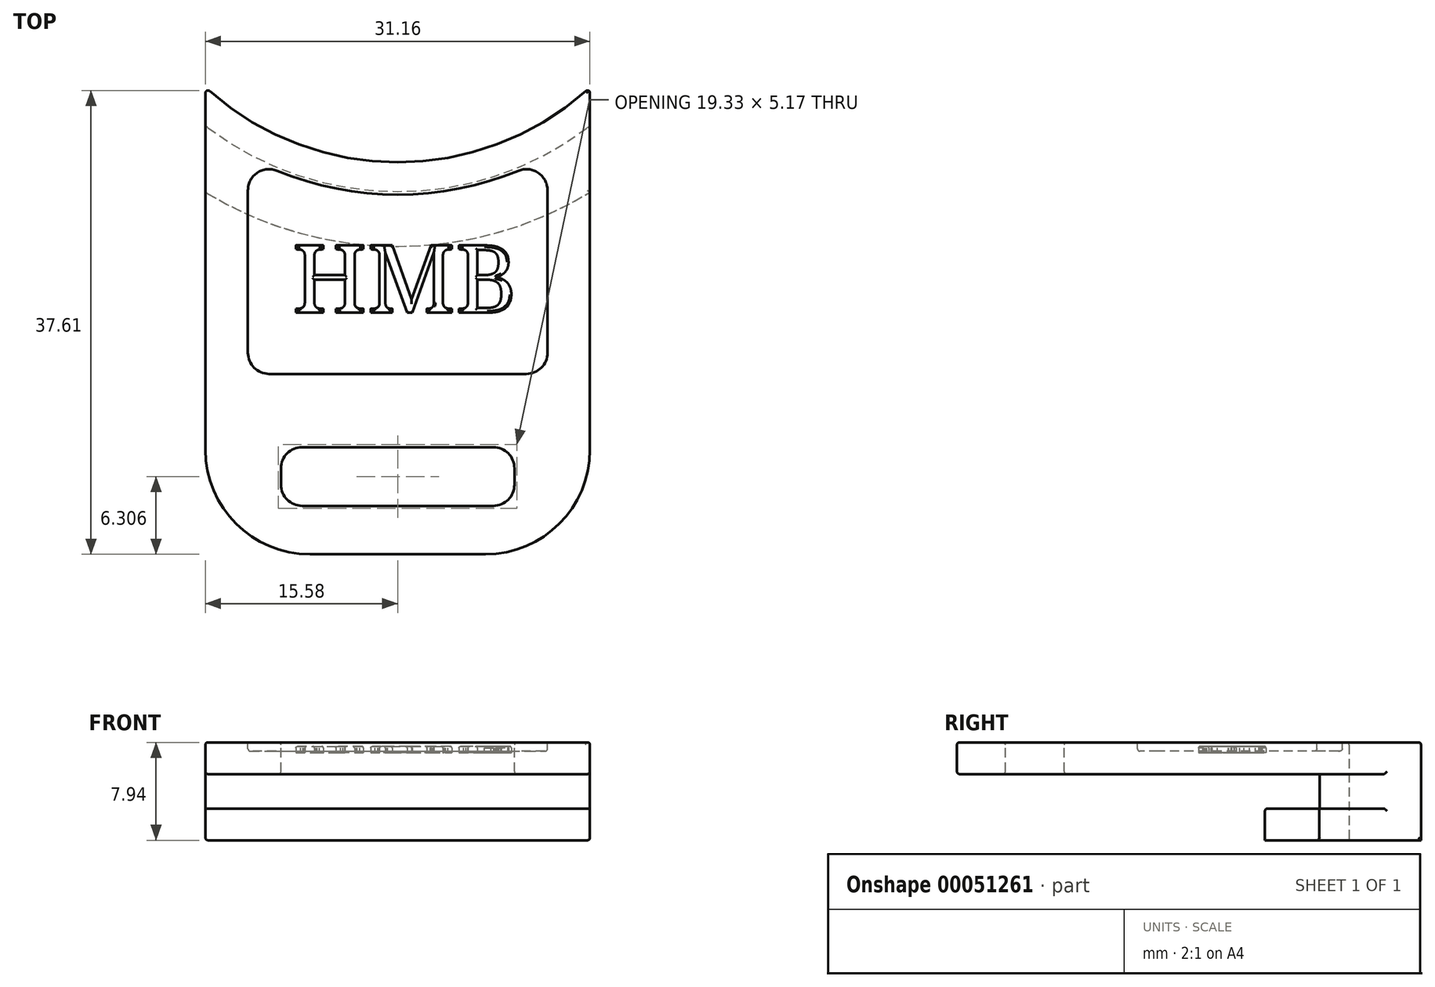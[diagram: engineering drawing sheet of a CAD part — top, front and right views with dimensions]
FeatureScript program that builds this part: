
annotation { "Feature Type Name" : "Feature", "Feature Type Description" : "" }
export const myFeature = defineFeature(function(context is Context, id is Id, definition is map)
    precondition{}
    {
        {
            var Q0;
            Q0=qCreatedBy(makeId("Top.planeOp"),FACE);
            var sketch = newSketch(context, id + "F0", { "sketchPlane" : qUnion([Q0])});
            skCircle(sketch, "E0", {"center": v(0, 0) * mm, "radius": 25.4 * mm});
            skCircle(sketch, "E1", {"center": v(0, 0) * mm, "radius": 63.5 * mm});
            skSolve(sketch);
        }
        {
            var Q0;
            Q0=qSketchRegion(id+"F0",true);
            extrude(context, id + "F1", {"entities" : qUnion([Q0]), "depth" : 2.8 * mm, "symmetric" : true});
        }
        {
            var Q0;
            Q0=qCreatedBy(makeId("Top.planeOp"),FACE);
            var sketch = newSketch(context, id + "F2", { "sketchPlane" : qUnion([Q0])});
            skCircle(sketch, "E2", {"center": v(0, 0) * mm, "radius": 23.02 * mm});
            skSolve(sketch);
        }
        {
            var Q0;
            Q0=qSketchRegion(id+"F2",true);
            extrude(context, id + "F3", {"entities" : qUnion([Q0]), "operationType" : NewBodyOperationType.ADD, "depth" : 27.94 * mm, "symmetric" : true});
        }
        {
            var Q0;
            Q0=qCreatedBy(makeId("Top.planeOp"),FACE);
            var sketch = newSketch(context, id + "F4", { "sketchPlane" : qUnion([Q0])});
            skLineSegment(sketch, "E3.bottom", {"start": v(-15.58, 0) * mm, "end": v(15.58, 0) * mm});
            skLineSegment(sketch, "E3.top", {"start": v(-7.12, -54.8) * mm, "end": v(7.12, -54.8) * mm});
            skLineSegment(sketch, "E3.left", {"start": v(-15.58, 0) * mm, "end": v(-15.58, -46.34) * mm});
            skLineSegment(sketch, "E3.right", {"start": v(15.58, 0) * mm, "end": v(15.58, -46.34) * mm});
            skPoint(sketch, "E4.visualSharp", {"position": v(-15.58, -54.8) * mm});
            skArc(sketch, "E4.filletArc", {"start": v(-15.58, -46.34) * mm, "mid": v(-13.1, -52.33) * mm, "end": v(-7.12, -54.8) * mm});
            skPoint(sketch, "E5.visualSharp", {"position": v(15.58, -54.8) * mm});
            skArc(sketch, "E5.filletArc", {"start": v(7.12, -54.8) * mm, "mid": v(13.1, -52.33) * mm, "end": v(15.58, -46.34) * mm});
            skLineSegment(sketch, "E6", {"start": v(0, 8.02) * mm, "end": v(0, -68.52) * mm, "construction": true});
            skSolve(sketch);
        }
        {
            var Q0;
            Q0=qSketchRegion(id+"F4",true);
            extrude(context, id + "F5", {"entities" : qUnion([Q0]), "depth" : 7.94 * mm, "symmetric" : true});
        }
        {
            var Q0;
            Q0=makeQuery(id+"F5.opExtrude","CAP_FACE",FACE,{"disambiguationData":[OSD([sQuery(id+"F4.wireOp",EDGE,"E3.bottom"),sQuery(id+"F4.wireOp",EDGE,"E3.top"),sQuery(id+"F4.wireOp",EDGE,"E3.left"),sQuery(id+"F4.wireOp",EDGE,"E3.right"),sQuery(id+"F4.wireOp",EDGE,"E4.filletArc"),sQuery(id+"F4.wireOp",EDGE,"E5.filletArc")])],"isStart":true});
            var sketch = newSketch(context, id + "F6", { "sketchPlane" : qUnion([Q0])});
            skCircle(sketch, "E7", {"center": v(0, 0) * mm, "radius": 29.85 * mm});
            skCircle(sketch, "E8", {"center": v(0, 0) * mm, "radius": 63.5 * mm});
            skSolve(sketch);
        }
        {
            var Q0;
            Q0=qSketchRegion(id+"F6",true);
            extrude(context, id + "F7", {"entities" : qUnion([Q0]), "oppositeDirection" : true, "depth" : 4.4 * mm});
        }
        {
            var Q0;
            Q0=makeQuery(id+"F5.opExtrude","CAP_FACE",FACE,{"disambiguationData":[OSD([sQuery(id+"F4.wireOp",EDGE,"E3.bottom"),sQuery(id+"F4.wireOp",EDGE,"E3.top"),sQuery(id+"F4.wireOp",EDGE,"E3.left"),sQuery(id+"F4.wireOp",EDGE,"E3.right"),sQuery(id+"F4.wireOp",EDGE,"E4.filletArc"),sQuery(id+"F4.wireOp",EDGE,"E5.filletArc")])],"isStart":false});
            var sketch = newSketch(context, id + "F8", { "sketchPlane" : qUnion([Q0])});
            skLineSegment(sketch, "E9.rect.bottom", {"start": v(7.75, -50.88) * mm, "end": v(-7.75, -50.88) * mm});
            skLineSegment(sketch, "E9.rect.top", {"start": v(7.75, -46.12) * mm, "end": v(-7.75, -46.12) * mm});
            skLineSegment(sketch, "E9.rect.left", {"start": v(9.46, -49.17) * mm, "end": v(9.46, -47.83) * mm});
            skLineSegment(sketch, "E9.rect.right", {"start": v(-9.46, -49.17) * mm, "end": v(-9.46, -47.83) * mm});
            skPoint(sketch, "E9.rect.middle", {"position": v(0, -48.5) * mm});
            skPoint(sketch, "E10.visualSharp", {"position": v(-9.46, -46.12) * mm});
            skArc(sketch, "E10.filletArc", {"start": v(-7.75, -46.12) * mm, "mid": v(-8.96, -46.62) * mm, "end": v(-9.46, -47.83) * mm});
            skPoint(sketch, "E11.visualSharp", {"position": v(-9.46, -50.88) * mm});
            skArc(sketch, "E11.filletArc", {"start": v(-9.46, -49.17) * mm, "mid": v(-8.96, -50.38) * mm, "end": v(-7.75, -50.88) * mm});
            skPoint(sketch, "E12.visualSharp", {"position": v(9.46, -46.12) * mm});
            skArc(sketch, "E12.filletArc", {"start": v(9.46, -47.83) * mm, "mid": v(8.96, -46.62) * mm, "end": v(7.75, -46.12) * mm});
            skPoint(sketch, "E13.visualSharp", {"position": v(9.46, -50.88) * mm});
            skArc(sketch, "E13.filletArc", {"start": v(7.75, -50.88) * mm, "mid": v(8.96, -50.38) * mm, "end": v(9.46, -49.17) * mm});
            skSolve(sketch);
        }
        {
            var Q0;
            Q0=qSketchRegion(id+"F8",true);
            var Q1;
            Q1=makeQuery(id+"F10.opBoolean","COPY",FACE,{"derivedFrom":makeQuery(id+"F1.opExtrude","CAP_FACE",FACE,{"disambiguationData":[OSD([sQuery(id+"F0.wireOp",EDGE,"E0"),sQuery(id+"F0.wireOp",EDGE,"E1")])],"isStart":false})});
            extrude(context, id + "F9", {"entities" : qUnion([Q0]), "operationType" : NewBodyOperationType.REMOVE, "oppositeDirection" : true, "endBoundEntityFace" : qUnion([Q1]), "depth" : 27.8 * mm, "symmetric" : true});
        }
        {
            var Q0;
            Q0=makeQuery(id+"F3.opExtrude","SWEPT_BODY",BODY,{"disambiguationData":[OSD([sQuery(id+"F2.wireOp",EDGE,"E2")])]});
            var Q1;
            Q1=makeQuery(id+"F7.opExtrude","SWEPT_BODY",BODY,{"disambiguationData":[OSD([sQuery(id+"F6.wireOp",EDGE,"E7"),sQuery(id+"F6.wireOp",EDGE,"E8")])]});
            var Q2;
            Q2=makeQuery(id+"F1.opExtrude","SWEPT_BODY",BODY,{"disambiguationData":[OSD([sQuery(id+"F0.wireOp",EDGE,"E0"),sQuery(id+"F0.wireOp",EDGE,"E1")])]});
            var Q3;
            Q3=makeQuery(id+"F5.opExtrude","SWEPT_BODY",BODY,{"disambiguationData":[OSD([sQuery(id+"F4.wireOp",EDGE,"E3.bottom"),sQuery(id+"F4.wireOp",EDGE,"E3.top"),sQuery(id+"F4.wireOp",EDGE,"E3.left"),sQuery(id+"F4.wireOp",EDGE,"E3.right"),sQuery(id+"F4.wireOp",EDGE,"E4.filletArc"),sQuery(id+"F4.wireOp",EDGE,"E5.filletArc")])]});
            booleanBodies(context, id + "F10", {"operationType" : BooleanOperationType.SUBTRACTION, "tools" : qUnion([Q0, Q1, Q2]), "targets" : qUnion([Q3])});
        }
        {
            var Q0;
            Q0=makeQuery(id+"F5.opExtrude","CAP_EDGE",EDGE,{"disambiguationData":[OSD([sQuery(id+"F4.wireOp",EDGE,"E3.right")])],"isStart":false});
            var Q1;
            Q1=makeQuery(id+"F10.opBoolean","INTERSECT",EDGE,{"derivedFrom":[makeQuery(id+"F3.opExtrude","SWEPT_FACE",FACE,{"disambiguationData":[OSD([sQuery(id+"F2.wireOp",EDGE,"E2")])]}),makeQuery(id+"F5.opExtrude","CAP_FACE",FACE,{"disambiguationData":[OSD([sQuery(id+"F4.wireOp",EDGE,"E3.bottom"),sQuery(id+"F4.wireOp",EDGE,"E3.top"),sQuery(id+"F4.wireOp",EDGE,"E3.left"),sQuery(id+"F4.wireOp",EDGE,"E3.right"),sQuery(id+"F4.wireOp",EDGE,"E4.filletArc"),sQuery(id+"F4.wireOp",EDGE,"E5.filletArc")])],"isStart":false})]});
            var Q2;
            Q2=makeQuery(id+"F5.opExtrude","CAP_EDGE",EDGE,{"disambiguationData":[OSD([sQuery(id+"F4.wireOp",EDGE,"E3.left")])],"isStart":false});
            var Q3;
            Q3=makeQuery(id+"F5.opExtrude","CAP_EDGE",EDGE,{"disambiguationData":[OSD([sQuery(id+"F4.wireOp",EDGE,"E4.filletArc")])],"isStart":false});
            var Q4;
            Q4=makeQuery(id+"F5.opExtrude","CAP_EDGE",EDGE,{"disambiguationData":[OSD([sQuery(id+"F4.wireOp",EDGE,"E3.top")])],"isStart":false});
            var Q5;
            Q5=makeQuery(id+"F5.opExtrude","CAP_EDGE",EDGE,{"disambiguationData":[OSD([sQuery(id+"F4.wireOp",EDGE,"E5.filletArc")])],"isStart":false});
            var Q6;
            Q6=makeQuery(id+"F10.opBoolean","INTERSECT",EDGE,{"derivedFrom":[makeQuery(id+"F1.opExtrude","CAP_FACE",FACE,{"disambiguationData":[OSD([sQuery(id+"F0.wireOp",EDGE,"E0"),sQuery(id+"F0.wireOp",EDGE,"E1")])],"isStart":false}),makeQuery(id+"F5.opExtrude","SWEPT_FACE",FACE,{"disambiguationData":[OSD([sQuery(id+"F4.wireOp",EDGE,"E3.right")])]})]});
            var Q7;
            Q7=makeQuery(id+"F10.opBoolean","INTERSECT",EDGE,{"derivedFrom":[makeQuery(id+"F1.opExtrude","CAP_FACE",FACE,{"disambiguationData":[OSD([sQuery(id+"F0.wireOp",EDGE,"E0"),sQuery(id+"F0.wireOp",EDGE,"E1")])],"isStart":false}),makeQuery(id+"F5.opExtrude","SWEPT_FACE",FACE,{"disambiguationData":[OSD([sQuery(id+"F4.wireOp",EDGE,"E5.filletArc")])]})]});
            var Q8;
            Q8=makeQuery(id+"F10.opBoolean","INTERSECT",EDGE,{"derivedFrom":[makeQuery(id+"F1.opExtrude","CAP_FACE",FACE,{"disambiguationData":[OSD([sQuery(id+"F0.wireOp",EDGE,"E0"),sQuery(id+"F0.wireOp",EDGE,"E1")])],"isStart":false}),makeQuery(id+"F5.opExtrude","SWEPT_FACE",FACE,{"disambiguationData":[OSD([sQuery(id+"F4.wireOp",EDGE,"E3.top")])]})]});
            var Q9;
            Q9=makeQuery(id+"F10.opBoolean","INTERSECT",EDGE,{"derivedFrom":[makeQuery(id+"F1.opExtrude","CAP_FACE",FACE,{"disambiguationData":[OSD([sQuery(id+"F0.wireOp",EDGE,"E0"),sQuery(id+"F0.wireOp",EDGE,"E1")])],"isStart":false}),makeQuery(id+"F5.opExtrude","SWEPT_FACE",FACE,{"disambiguationData":[OSD([sQuery(id+"F4.wireOp",EDGE,"E4.filletArc")])]})]});
            var Q10;
            Q10=makeQuery(id+"F10.opBoolean","INTERSECT",EDGE,{"derivedFrom":[makeQuery(id+"F1.opExtrude","CAP_FACE",FACE,{"disambiguationData":[OSD([sQuery(id+"F0.wireOp",EDGE,"E0"),sQuery(id+"F0.wireOp",EDGE,"E1")])],"isStart":false}),makeQuery(id+"F5.opExtrude","SWEPT_FACE",FACE,{"disambiguationData":[OSD([sQuery(id+"F4.wireOp",EDGE,"E3.left")])]})]});
            var Q11;
            Q11=makeQuery(id+"F10.opBoolean","INTERSECT",EDGE,{"derivedFrom":[makeQuery(id+"F1.opExtrude","SWEPT_FACE",FACE,{"disambiguationData":[OSD([sQuery(id+"F0.wireOp",EDGE,"E0")])]}),makeQuery(id+"F5.opExtrude","SWEPT_FACE",FACE,{"disambiguationData":[OSD([sQuery(id+"F4.wireOp",EDGE,"E3.left")])]})]});
            var Q12;
            Q12=makeQuery(id+"F10.opBoolean","INTERSECT",EDGE,{"derivedFrom":[makeQuery(id+"F1.opExtrude","CAP_FACE",FACE,{"disambiguationData":[OSD([sQuery(id+"F0.wireOp",EDGE,"E0"),sQuery(id+"F0.wireOp",EDGE,"E1")])],"isStart":true}),makeQuery(id+"F5.opExtrude","SWEPT_FACE",FACE,{"disambiguationData":[OSD([sQuery(id+"F4.wireOp",EDGE,"E3.left")])]})]});
            var Q13;
            Q13=makeQuery(id+"F10.opBoolean","INTERSECT",EDGE,{"derivedFrom":[makeQuery(id+"F5.opExtrude","SWEPT_FACE",FACE,{"disambiguationData":[OSD([sQuery(id+"F4.wireOp",EDGE,"E3.left")])]}),makeQuery(id+"F7.opExtrude","SWEPT_FACE",FACE,{"disambiguationData":[OSD([sQuery(id+"F6.wireOp",EDGE,"E7")])]})]});
            var Q14;
            Q14=makeQuery(id+"F10.opBoolean","INTERSECT",EDGE,{"derivedFrom":[makeQuery(id+"F1.opExtrude","CAP_FACE",FACE,{"disambiguationData":[OSD([sQuery(id+"F0.wireOp",EDGE,"E0"),sQuery(id+"F0.wireOp",EDGE,"E1")])],"isStart":true}),makeQuery(id+"F7.opExtrude","SWEPT_FACE",FACE,{"disambiguationData":[OSD([sQuery(id+"F6.wireOp",EDGE,"E7")])]})]});
            var Q15;
            Q15=makeQuery(id+"F10.opBoolean","COPY",EDGE,{"derivedFrom":makeQuery(id+"F7.opExtrude","CAP_EDGE",EDGE,{"disambiguationData":[OSD([sQuery(id+"F6.wireOp",EDGE,"E7")])],"isStart":true})});
            var Q16;
            Q16=makeQuery(id+"F5.opExtrude","CAP_EDGE",EDGE,{"disambiguationData":[OSD([sQuery(id+"F4.wireOp",EDGE,"E3.left")])],"isStart":true});
            var Q17;
            Q17=makeQuery(id+"F10.opBoolean","INTERSECT",EDGE,{"derivedFrom":[makeQuery(id+"F3.opExtrude","SWEPT_FACE",FACE,{"disambiguationData":[OSD([sQuery(id+"F2.wireOp",EDGE,"E2")])]}),makeQuery(id+"F5.opExtrude","SWEPT_FACE",FACE,{"disambiguationData":[OSD([sQuery(id+"F4.wireOp",EDGE,"E3.left")])]})]});
            var Q18;
            Q18=makeQuery(id+"F5.opExtrude","CAP_EDGE",EDGE,{"disambiguationData":[OSD([sQuery(id+"F4.wireOp",EDGE,"E3.right")])],"isStart":true});
            var Q19;
            Q19=makeQuery(id+"F10.opBoolean","INTERSECT",EDGE,{"derivedFrom":[makeQuery(id+"F1.opExtrude","CAP_FACE",FACE,{"disambiguationData":[OSD([sQuery(id+"F0.wireOp",EDGE,"E0"),sQuery(id+"F0.wireOp",EDGE,"E1")])],"isStart":true}),makeQuery(id+"F5.opExtrude","SWEPT_FACE",FACE,{"disambiguationData":[OSD([sQuery(id+"F4.wireOp",EDGE,"E3.right")])]})]});
            var Q20;
            Q20=makeQuery(id+"F10.opBoolean","INTERSECT",EDGE,{"derivedFrom":[makeQuery(id+"F1.opExtrude","SWEPT_FACE",FACE,{"disambiguationData":[OSD([sQuery(id+"F0.wireOp",EDGE,"E0")])]}),makeQuery(id+"F5.opExtrude","SWEPT_FACE",FACE,{"disambiguationData":[OSD([sQuery(id+"F4.wireOp",EDGE,"E3.right")])]})]});
            var Q21;
            Q21=makeQuery(id+"F10.opBoolean","INTERSECT",EDGE,{"derivedFrom":[makeQuery(id+"F3.opExtrude","SWEPT_FACE",FACE,{"disambiguationData":[OSD([sQuery(id+"F2.wireOp",EDGE,"E2")])]}),makeQuery(id+"F5.opExtrude","SWEPT_FACE",FACE,{"disambiguationData":[OSD([sQuery(id+"F4.wireOp",EDGE,"E3.right")])]})]});
            var Q22;
            Q22=makeQuery(id+"F5.opExtrude","CAP_FACE",FACE,{"disambiguationData":[OSD([sQuery(id+"F4.wireOp",EDGE,"E3.bottom"),sQuery(id+"F4.wireOp",EDGE,"E3.top"),sQuery(id+"F4.wireOp",EDGE,"E3.left"),sQuery(id+"F4.wireOp",EDGE,"E3.right"),sQuery(id+"F4.wireOp",EDGE,"E4.filletArc"),sQuery(id+"F4.wireOp",EDGE,"E5.filletArc")])],"isStart":false});
            var Q23;
            Q23=makeQuery(id+"F9.boolean.opBoolean","INTERSECT",EDGE,{"derivedFrom":[makeQuery(id+"F5.opExtrude","CAP_FACE",FACE,{"disambiguationData":[OSD([sQuery(id+"F4.wireOp",EDGE,"E3.bottom"),sQuery(id+"F4.wireOp",EDGE,"E3.top"),sQuery(id+"F4.wireOp",EDGE,"E3.left"),sQuery(id+"F4.wireOp",EDGE,"E3.right"),sQuery(id+"F4.wireOp",EDGE,"E4.filletArc"),sQuery(id+"F4.wireOp",EDGE,"E5.filletArc")])],"isStart":false}),makeQuery(id+"F9.opExtrude","SWEPT_FACE",FACE,{"disambiguationData":[OSD([sQuery(id+"F8.wireOp",EDGE,"E10.filletArc")])]})]});
            var Q24;
            Q24=makeQuery(id+"F9.boolean.opBoolean","INTERSECT",EDGE,{"derivedFrom":[makeQuery(id+"F5.opExtrude","CAP_FACE",FACE,{"disambiguationData":[OSD([sQuery(id+"F4.wireOp",EDGE,"E3.bottom"),sQuery(id+"F4.wireOp",EDGE,"E3.top"),sQuery(id+"F4.wireOp",EDGE,"E3.left"),sQuery(id+"F4.wireOp",EDGE,"E3.right"),sQuery(id+"F4.wireOp",EDGE,"E4.filletArc"),sQuery(id+"F4.wireOp",EDGE,"E5.filletArc")])],"isStart":false}),makeQuery(id+"F9.opExtrude","SWEPT_FACE",FACE,{"disambiguationData":[OSD([sQuery(id+"F8.wireOp",EDGE,"E11.filletArc")])]})]});
            var Q25;
            Q25=makeQuery(id+"F9.boolean.opBoolean","INTERSECT",EDGE,{"derivedFrom":[makeQuery(id+"F5.opExtrude","CAP_FACE",FACE,{"disambiguationData":[OSD([sQuery(id+"F4.wireOp",EDGE,"E3.bottom"),sQuery(id+"F4.wireOp",EDGE,"E3.top"),sQuery(id+"F4.wireOp",EDGE,"E3.left"),sQuery(id+"F4.wireOp",EDGE,"E3.right"),sQuery(id+"F4.wireOp",EDGE,"E4.filletArc"),sQuery(id+"F4.wireOp",EDGE,"E5.filletArc")])],"isStart":false}),makeQuery(id+"F9.opExtrude","SWEPT_FACE",FACE,{"disambiguationData":[OSD([sQuery(id+"F8.wireOp",EDGE,"E9.rect.bottom")])]})]});
            var Q26;
            Q26=makeQuery(id+"F9.boolean.opBoolean","INTERSECT",EDGE,{"derivedFrom":[makeQuery(id+"F5.opExtrude","CAP_FACE",FACE,{"disambiguationData":[OSD([sQuery(id+"F4.wireOp",EDGE,"E3.bottom"),sQuery(id+"F4.wireOp",EDGE,"E3.top"),sQuery(id+"F4.wireOp",EDGE,"E3.left"),sQuery(id+"F4.wireOp",EDGE,"E3.right"),sQuery(id+"F4.wireOp",EDGE,"E4.filletArc"),sQuery(id+"F4.wireOp",EDGE,"E5.filletArc")])],"isStart":false}),makeQuery(id+"F9.opExtrude","SWEPT_FACE",FACE,{"disambiguationData":[OSD([sQuery(id+"F8.wireOp",EDGE,"E9.rect.right")])]})]});
            var Q27;
            Q27=makeQuery(id+"F9.boolean.opBoolean","INTERSECT",EDGE,{"derivedFrom":[makeQuery(id+"F5.opExtrude","CAP_FACE",FACE,{"disambiguationData":[OSD([sQuery(id+"F4.wireOp",EDGE,"E3.bottom"),sQuery(id+"F4.wireOp",EDGE,"E3.top"),sQuery(id+"F4.wireOp",EDGE,"E3.left"),sQuery(id+"F4.wireOp",EDGE,"E3.right"),sQuery(id+"F4.wireOp",EDGE,"E4.filletArc"),sQuery(id+"F4.wireOp",EDGE,"E5.filletArc")])],"isStart":false}),makeQuery(id+"F9.opExtrude","SWEPT_FACE",FACE,{"disambiguationData":[OSD([sQuery(id+"F8.wireOp",EDGE,"E9.rect.top")])]})]});
            var Q28;
            Q28=makeQuery(id+"F9.boolean.opBoolean","INTERSECT",EDGE,{"derivedFrom":[makeQuery(id+"F5.opExtrude","CAP_FACE",FACE,{"disambiguationData":[OSD([sQuery(id+"F4.wireOp",EDGE,"E3.bottom"),sQuery(id+"F4.wireOp",EDGE,"E3.top"),sQuery(id+"F4.wireOp",EDGE,"E3.left"),sQuery(id+"F4.wireOp",EDGE,"E3.right"),sQuery(id+"F4.wireOp",EDGE,"E4.filletArc"),sQuery(id+"F4.wireOp",EDGE,"E5.filletArc")])],"isStart":false}),makeQuery(id+"F9.opExtrude","SWEPT_FACE",FACE,{"disambiguationData":[OSD([sQuery(id+"F8.wireOp",EDGE,"E12.filletArc")])]})]});
            var Q29;
            Q29=makeQuery(id+"F9.boolean.opBoolean","INTERSECT",EDGE,{"derivedFrom":[makeQuery(id+"F5.opExtrude","CAP_FACE",FACE,{"disambiguationData":[OSD([sQuery(id+"F4.wireOp",EDGE,"E3.bottom"),sQuery(id+"F4.wireOp",EDGE,"E3.top"),sQuery(id+"F4.wireOp",EDGE,"E3.left"),sQuery(id+"F4.wireOp",EDGE,"E3.right"),sQuery(id+"F4.wireOp",EDGE,"E4.filletArc"),sQuery(id+"F4.wireOp",EDGE,"E5.filletArc")])],"isStart":false}),makeQuery(id+"F9.opExtrude","SWEPT_FACE",FACE,{"disambiguationData":[OSD([sQuery(id+"F8.wireOp",EDGE,"E13.filletArc")])]})]});
            var Q30;
            Q30=makeQuery(id+"F9.boolean.opBoolean","INTERSECT",EDGE,{"derivedFrom":[makeQuery(id+"F5.opExtrude","CAP_FACE",FACE,{"disambiguationData":[OSD([sQuery(id+"F4.wireOp",EDGE,"E3.bottom"),sQuery(id+"F4.wireOp",EDGE,"E3.top"),sQuery(id+"F4.wireOp",EDGE,"E3.left"),sQuery(id+"F4.wireOp",EDGE,"E3.right"),sQuery(id+"F4.wireOp",EDGE,"E4.filletArc"),sQuery(id+"F4.wireOp",EDGE,"E5.filletArc")])],"isStart":false}),makeQuery(id+"F9.opExtrude","SWEPT_FACE",FACE,{"disambiguationData":[OSD([sQuery(id+"F8.wireOp",EDGE,"E9.rect.left")])]})]});
            var Q31;
            Q31=makeQuery(id+"F10.opBoolean","INTERSECT",EDGE,{"derivedFrom":[makeQuery(id+"F1.opExtrude","CAP_FACE",FACE,{"disambiguationData":[OSD([sQuery(id+"F0.wireOp",EDGE,"E0"),sQuery(id+"F0.wireOp",EDGE,"E1")])],"isStart":false}),makeQuery(id+"F9.boolean.opBoolean","COPY",FACE,{"derivedFrom":makeQuery(id+"F9.opExtrude","SWEPT_FACE",FACE,{"disambiguationData":[OSD([sQuery(id+"F8.wireOp",EDGE,"E9.rect.top")])]})})]});
            var Q32;
            Q32=makeQuery(id+"F10.opBoolean","INTERSECT",EDGE,{"derivedFrom":[makeQuery(id+"F1.opExtrude","CAP_FACE",FACE,{"disambiguationData":[OSD([sQuery(id+"F0.wireOp",EDGE,"E0"),sQuery(id+"F0.wireOp",EDGE,"E1")])],"isStart":false}),makeQuery(id+"F9.boolean.opBoolean","COPY",FACE,{"derivedFrom":makeQuery(id+"F9.opExtrude","SWEPT_FACE",FACE,{"disambiguationData":[OSD([sQuery(id+"F8.wireOp",EDGE,"E10.filletArc")])]})})]});
            var Q33;
            Q33=makeQuery(id+"F10.opBoolean","INTERSECT",EDGE,{"derivedFrom":[makeQuery(id+"F1.opExtrude","CAP_FACE",FACE,{"disambiguationData":[OSD([sQuery(id+"F0.wireOp",EDGE,"E0"),sQuery(id+"F0.wireOp",EDGE,"E1")])],"isStart":false}),makeQuery(id+"F9.boolean.opBoolean","COPY",FACE,{"derivedFrom":makeQuery(id+"F9.opExtrude","SWEPT_FACE",FACE,{"disambiguationData":[OSD([sQuery(id+"F8.wireOp",EDGE,"E9.rect.right")])]})})]});
            var Q34;
            Q34=makeQuery(id+"F10.opBoolean","INTERSECT",EDGE,{"derivedFrom":[makeQuery(id+"F1.opExtrude","CAP_FACE",FACE,{"disambiguationData":[OSD([sQuery(id+"F0.wireOp",EDGE,"E0"),sQuery(id+"F0.wireOp",EDGE,"E1")])],"isStart":false}),makeQuery(id+"F9.boolean.opBoolean","COPY",FACE,{"derivedFrom":makeQuery(id+"F9.opExtrude","SWEPT_FACE",FACE,{"disambiguationData":[OSD([sQuery(id+"F8.wireOp",EDGE,"E11.filletArc")])]})})]});
            var Q35;
            Q35=makeQuery(id+"F10.opBoolean","INTERSECT",EDGE,{"derivedFrom":[makeQuery(id+"F1.opExtrude","CAP_FACE",FACE,{"disambiguationData":[OSD([sQuery(id+"F0.wireOp",EDGE,"E0"),sQuery(id+"F0.wireOp",EDGE,"E1")])],"isStart":false}),makeQuery(id+"F9.boolean.opBoolean","COPY",FACE,{"derivedFrom":makeQuery(id+"F9.opExtrude","SWEPT_FACE",FACE,{"disambiguationData":[OSD([sQuery(id+"F8.wireOp",EDGE,"E9.rect.bottom")])]})})]});
            var Q36;
            Q36=makeQuery(id+"F10.opBoolean","INTERSECT",EDGE,{"derivedFrom":[makeQuery(id+"F1.opExtrude","CAP_FACE",FACE,{"disambiguationData":[OSD([sQuery(id+"F0.wireOp",EDGE,"E0"),sQuery(id+"F0.wireOp",EDGE,"E1")])],"isStart":false}),makeQuery(id+"F9.boolean.opBoolean","COPY",FACE,{"derivedFrom":makeQuery(id+"F9.opExtrude","SWEPT_FACE",FACE,{"disambiguationData":[OSD([sQuery(id+"F8.wireOp",EDGE,"E13.filletArc")])]})})]});
            var Q37;
            Q37=makeQuery(id+"F10.opBoolean","INTERSECT",EDGE,{"derivedFrom":[makeQuery(id+"F1.opExtrude","CAP_FACE",FACE,{"disambiguationData":[OSD([sQuery(id+"F0.wireOp",EDGE,"E0"),sQuery(id+"F0.wireOp",EDGE,"E1")])],"isStart":false}),makeQuery(id+"F9.boolean.opBoolean","COPY",FACE,{"derivedFrom":makeQuery(id+"F9.opExtrude","SWEPT_FACE",FACE,{"disambiguationData":[OSD([sQuery(id+"F8.wireOp",EDGE,"E9.rect.left")])]})})]});
            var Q38;
            Q38=makeQuery(id+"F10.opBoolean","INTERSECT",EDGE,{"derivedFrom":[makeQuery(id+"F1.opExtrude","CAP_FACE",FACE,{"disambiguationData":[OSD([sQuery(id+"F0.wireOp",EDGE,"E0"),sQuery(id+"F0.wireOp",EDGE,"E1")])],"isStart":false}),makeQuery(id+"F9.boolean.opBoolean","COPY",FACE,{"derivedFrom":makeQuery(id+"F9.opExtrude","SWEPT_FACE",FACE,{"disambiguationData":[OSD([sQuery(id+"F8.wireOp",EDGE,"E12.filletArc")])]})})]});
            fillet(context, id + "F11", {"entities" : qUnion([Q0, Q1, Q2, Q3, Q4, Q5, Q6, Q7, Q8, Q9, Q10, Q11, Q12, Q13, Q14, Q15, Q16, Q17, Q18, Q19, Q20, Q21, Q22, Q23, Q24, Q25, Q26, Q27, Q28, Q29, Q30, Q31, Q32, Q33, Q34, Q35, Q36, Q37, Q38]), "radius" : 0.2 * mm, "tangentPropagation" : true, "allowEdgeOverflow" : false});
        }
        {
            var Q0;
            Q0=makeQuery(id+"F5.opExtrude","CAP_FACE",FACE,{"disambiguationData":[OSD([sQuery(id+"F4.wireOp",EDGE,"E3.bottom"),sQuery(id+"F4.wireOp",EDGE,"E3.top"),sQuery(id+"F4.wireOp",EDGE,"E3.left"),sQuery(id+"F4.wireOp",EDGE,"E3.right"),sQuery(id+"F4.wireOp",EDGE,"E4.filletArc"),sQuery(id+"F4.wireOp",EDGE,"E5.filletArc")])],"isStart":false});
            var sketch = newSketch(context, id + "F12", { "sketchPlane" : qUnion([Q0])});
            skArc(sketch, "E14", {"start": v(-9.77, -23.71) * mm, "mid": v(0, -25.65) * mm, "end": v(9.77, -23.71) * mm});
            skLineSegment(sketch, "E15", {"start": v(-12.14, -25.3) * mm, "end": v(-12.14, -38.47) * mm});
            skLineSegment(sketch, "E16", {"start": v(-10.43, -40.18) * mm, "end": v(10.43, -40.18) * mm});
            skLineSegment(sketch, "E17", {"start": v(12.14, -38.47) * mm, "end": v(12.14, -25.3) * mm});
            skPoint(sketch, "E18.visualSharp", {"position": v(-12.14, -40.18) * mm});
            skArc(sketch, "E18.filletArc", {"start": v(-12.14, -38.47) * mm, "mid": v(-11.64, -39.68) * mm, "end": v(-10.43, -40.18) * mm});
            skPoint(sketch, "E19.visualSharp", {"position": v(12.14, -40.18) * mm});
            skArc(sketch, "E19.filletArc", {"start": v(10.43, -40.18) * mm, "mid": v(11.64, -39.68) * mm, "end": v(12.14, -38.47) * mm});
            skPoint(sketch, "E20.visualSharp", {"position": v(12.14, -22.6) * mm});
            skArc(sketch, "E20.filletArc", {"start": v(12.14, -25.3) * mm, "mid": v(11.38, -23.87) * mm, "end": v(9.77, -23.71) * mm});
            skPoint(sketch, "E21.visualSharp", {"position": v(-12.14, -22.6) * mm});
            skArc(sketch, "E21.filletArc", {"start": v(-9.77, -23.71) * mm, "mid": v(-11.38, -23.87) * mm, "end": v(-12.14, -25.3) * mm});
            skSolve(sketch);
        }
        {
            var Q0;
            Q0=qSketchRegion(id+"F12",true);
            extrude(context, id + "F13", {"entities" : qUnion([Q0]), "operationType" : NewBodyOperationType.REMOVE, "oppositeDirection" : true, "depth" : 0.71 * mm});
        }
        {
            var Q0;
            Q0=makeQuery(id+"F13.boolean.opBoolean","COPY",FACE,{"derivedFrom":makeQuery(id+"F13.opExtrude","CAP_FACE",FACE,{"disambiguationData":[OSD([sQuery(id+"F12.wireOp",EDGE,"E14"),sQuery(id+"F12.wireOp",EDGE,"E15"),sQuery(id+"F12.wireOp",EDGE,"E16"),sQuery(id+"F12.wireOp",EDGE,"E17"),sQuery(id+"F12.wireOp",EDGE,"E18.filletArc"),sQuery(id+"F12.wireOp",EDGE,"E19.filletArc"),sQuery(id+"F12.wireOp",EDGE,"E20.filletArc"),sQuery(id+"F12.wireOp",EDGE,"E21.filletArc")])],"isStart":false})});
            var Q1;
            Q1=makeQuery(id+"F13.boolean.opBoolean","COPY",EDGE,{"derivedFrom":makeQuery(id+"F13.opExtrude","CAP_EDGE",EDGE,{"disambiguationData":[OSD([sQuery(id+"F12.wireOp",EDGE,"E15")])],"isStart":true})});
            var Q2;
            Q2=makeQuery(id+"F13.boolean.opBoolean","COPY",EDGE,{"derivedFrom":makeQuery(id+"F13.opExtrude","CAP_EDGE",EDGE,{"disambiguationData":[OSD([sQuery(id+"F12.wireOp",EDGE,"E21.filletArc")])],"isStart":true})});
            var Q3;
            Q3=makeQuery(id+"F13.boolean.opBoolean","COPY",EDGE,{"derivedFrom":makeQuery(id+"F13.opExtrude","CAP_EDGE",EDGE,{"disambiguationData":[OSD([sQuery(id+"F12.wireOp",EDGE,"E14")])],"isStart":true})});
            var Q4;
            Q4=makeQuery(id+"F13.boolean.opBoolean","COPY",EDGE,{"derivedFrom":makeQuery(id+"F13.opExtrude","CAP_EDGE",EDGE,{"disambiguationData":[OSD([sQuery(id+"F12.wireOp",EDGE,"E20.filletArc")])],"isStart":true})});
            var Q5;
            Q5=makeQuery(id+"F13.boolean.opBoolean","COPY",EDGE,{"derivedFrom":makeQuery(id+"F13.opExtrude","CAP_EDGE",EDGE,{"disambiguationData":[OSD([sQuery(id+"F12.wireOp",EDGE,"E17")])],"isStart":true})});
            var Q6;
            Q6=makeQuery(id+"F13.boolean.opBoolean","COPY",EDGE,{"derivedFrom":makeQuery(id+"F13.opExtrude","CAP_EDGE",EDGE,{"disambiguationData":[OSD([sQuery(id+"F12.wireOp",EDGE,"E19.filletArc")])],"isStart":true})});
            var Q7;
            Q7=makeQuery(id+"F13.boolean.opBoolean","COPY",EDGE,{"derivedFrom":makeQuery(id+"F13.opExtrude","CAP_EDGE",EDGE,{"disambiguationData":[OSD([sQuery(id+"F12.wireOp",EDGE,"E16")])],"isStart":true})});
            var Q8;
            Q8=makeQuery(id+"F13.boolean.opBoolean","COPY",EDGE,{"derivedFrom":makeQuery(id+"F13.opExtrude","CAP_EDGE",EDGE,{"disambiguationData":[OSD([sQuery(id+"F12.wireOp",EDGE,"E18.filletArc")])],"isStart":true})});
            fillet(context, id + "F14", {"entities" : qUnion([Q0, Q1, Q2, Q3, Q4, Q5, Q6, Q7, Q8]), "radius" : 0.2 * mm, "tangentPropagation" : true, "allowEdgeOverflow" : false});
        }
        {
            var Q0;
            Q0=makeQuery(id+"F12.imprint","IMPRINT",FACE,{"disambiguationData":[TD([[makeQuery(id+"F12.imprint","IMPRINT",EDGE,{"derivedFrom":sQuery(id+"F12.wireOp",EDGE,"E14")}),-1.0]])]});
            var sketch = newSketch(context, id + "F15", { "sketchPlane" : qUnion([Q0])});
            skText(sketch, "E22", { "text": "HMB", "fontName": "NotoSerif-Regular.ttf"});
            const initialGuessF15  = {"E22": [0, -0.0055, 1, 0, 0.0055]};
            skSetInitialGuess(sketch, initialGuessF15);
            skSolve(sketch);
        }
        {
            var Q0;
            Q0=qSketchRegion(id+"F15",true);
            extrude(context, id + "F16", {"entities" : qUnion([Q0]), "depth" : 0.5 * mm});
        }
        {
            var Q0;
            Q0=makeQuery(id+"F16.opExtrude","SWEPT_BODY",BODY,{"disambiguationData":[OSD([sQuery(id+"F15.wireOp",EDGE,"E22.sketch_text.stroke-0"),sQuery(id+"F15.wireOp",EDGE,"E22.sketch_text.stroke-1"),sQuery(id+"F15.wireOp",EDGE,"E22.sketch_text.stroke-2"),sQuery(id+"F15.wireOp",EDGE,"E22.sketch_text.stroke-3"),sQuery(id+"F15.wireOp",EDGE,"E22.sketch_text.stroke-4"),sQuery(id+"F15.wireOp",EDGE,"E22.sketch_text.stroke-5"),sQuery(id+"F15.wireOp",EDGE,"E22.sketch_text.stroke-6"),sQuery(id+"F15.wireOp",EDGE,"E22.sketch_text.stroke-7"),sQuery(id+"F15.wireOp",EDGE,"E22.sketch_text.stroke-8"),sQuery(id+"F15.wireOp",EDGE,"E22.sketch_text.stroke-9"),sQuery(id+"F15.wireOp",EDGE,"E22.sketch_text.stroke-10"),sQuery(id+"F15.wireOp",EDGE,"E22.sketch_text.stroke-11"),sQuery(id+"F15.wireOp",EDGE,"E22.sketch_text.stroke-12"),sQuery(id+"F15.wireOp",EDGE,"E22.sketch_text.stroke-13"),sQuery(id+"F15.wireOp",EDGE,"E22.sketch_text.stroke-14"),sQuery(id+"F15.wireOp",EDGE,"E22.sketch_text.stroke-15"),sQuery(id+"F15.wireOp",EDGE,"E22.sketch_text.stroke-16"),sQuery(id+"F15.wireOp",EDGE,"E22.sketch_text.stroke-17"),sQuery(id+"F15.wireOp",EDGE,"E22.sketch_text.stroke-18"),sQuery(id+"F15.wireOp",EDGE,"E22.sketch_text.stroke-19"),sQuery(id+"F15.wireOp",EDGE,"E22.sketch_text.stroke-20"),sQuery(id+"F15.wireOp",EDGE,"E22.sketch_text.stroke-21"),sQuery(id+"F15.wireOp",EDGE,"E22.sketch_text.stroke-22"),sQuery(id+"F15.wireOp",EDGE,"E22.sketch_text.stroke-23"),sQuery(id+"F15.wireOp",EDGE,"E22.sketch_text.stroke-24"),sQuery(id+"F15.wireOp",EDGE,"E22.sketch_text.stroke-25"),sQuery(id+"F15.wireOp",EDGE,"E22.sketch_text.stroke-26"),sQuery(id+"F15.wireOp",EDGE,"E22.sketch_text.stroke-27"),sQuery(id+"F15.wireOp",EDGE,"E22.sketch_text.stroke-28"),sQuery(id+"F15.wireOp",EDGE,"E22.sketch_text.stroke-29"),sQuery(id+"F15.wireOp",EDGE,"E22.sketch_text.stroke-30"),sQuery(id+"F15.wireOp",EDGE,"E22.sketch_text.stroke-31"),sQuery(id+"F15.wireOp",EDGE,"E22.sketch_text.stroke-32"),sQuery(id+"F15.wireOp",EDGE,"E22.sketch_text.stroke-33"),sQuery(id+"F15.wireOp",EDGE,"E22.sketch_text.stroke-34"),sQuery(id+"F15.wireOp",EDGE,"E22.sketch_text.stroke-35"),sQuery(id+"F15.wireOp",EDGE,"E22.sketch_text.stroke-36"),sQuery(id+"F15.wireOp",EDGE,"E22.sketch_text.stroke-37"),sQuery(id+"F15.wireOp",EDGE,"E22.sketch_text.stroke-38"),sQuery(id+"F15.wireOp",EDGE,"E22.sketch_text.stroke-39"),sQuery(id+"F15.wireOp",EDGE,"E22.sketch_text.stroke-40"),sQuery(id+"F15.wireOp",EDGE,"E22.sketch_text.stroke-41"),sQuery(id+"F15.wireOp",EDGE,"E22.sketch_text.stroke-42"),sQuery(id+"F15.wireOp",EDGE,"E22.sketch_text.stroke-43"),sQuery(id+"F15.wireOp",EDGE,"E22.sketch_text.stroke-44"),sQuery(id+"F15.wireOp",EDGE,"E22.sketch_text.stroke-45"),sQuery(id+"F15.wireOp",EDGE,"E22.sketch_text.stroke-46"),sQuery(id+"F15.wireOp",EDGE,"E22.sketch_text.stroke-47"),sQuery(id+"F15.wireOp",EDGE,"E22.sketch_text.stroke-48"),sQuery(id+"F15.wireOp",EDGE,"E22.sketch_text.stroke-49"),sQuery(id+"F15.wireOp",EDGE,"E22.sketch_text.stroke-50"),sQuery(id+"F15.wireOp",EDGE,"E22.sketch_text.stroke-51"),sQuery(id+"F15.wireOp",EDGE,"E22.sketch_text.stroke-52"),sQuery(id+"F15.wireOp",EDGE,"E22.sketch_text.stroke-53"),sQuery(id+"F15.wireOp",EDGE,"E22.sketch_text.stroke-54"),sQuery(id+"F15.wireOp",EDGE,"E22.sketch_text.stroke-55"),sQuery(id+"F15.wireOp",EDGE,"E22.sketch_text.stroke-56"),sQuery(id+"F15.wireOp",EDGE,"E22.sketch_text.stroke-57"),sQuery(id+"F15.wireOp",EDGE,"E22.sketch_text.stroke-58"),sQuery(id+"F15.wireOp",EDGE,"E22.sketch_text.stroke-59")])]});
            var Q1;
            Q1=makeQuery(id+"F16.opExtrude","SWEPT_BODY",BODY,{"disambiguationData":[OSD([sQuery(id+"F15.wireOp",EDGE,"E22.sketch_text.stroke-60"),sQuery(id+"F15.wireOp",EDGE,"E22.sketch_text.stroke-61"),sQuery(id+"F15.wireOp",EDGE,"E22.sketch_text.stroke-62"),sQuery(id+"F15.wireOp",EDGE,"E22.sketch_text.stroke-63"),sQuery(id+"F15.wireOp",EDGE,"E22.sketch_text.stroke-64"),sQuery(id+"F15.wireOp",EDGE,"E22.sketch_text.stroke-65"),sQuery(id+"F15.wireOp",EDGE,"E22.sketch_text.stroke-66"),sQuery(id+"F15.wireOp",EDGE,"E22.sketch_text.stroke-67"),sQuery(id+"F15.wireOp",EDGE,"E22.sketch_text.stroke-68"),sQuery(id+"F15.wireOp",EDGE,"E22.sketch_text.stroke-69"),sQuery(id+"F15.wireOp",EDGE,"E22.sketch_text.stroke-70"),sQuery(id+"F15.wireOp",EDGE,"E22.sketch_text.stroke-71"),sQuery(id+"F15.wireOp",EDGE,"E22.sketch_text.stroke-72"),sQuery(id+"F15.wireOp",EDGE,"E22.sketch_text.stroke-73"),sQuery(id+"F15.wireOp",EDGE,"E22.sketch_text.stroke-74"),sQuery(id+"F15.wireOp",EDGE,"E22.sketch_text.stroke-75"),sQuery(id+"F15.wireOp",EDGE,"E22.sketch_text.stroke-76"),sQuery(id+"F15.wireOp",EDGE,"E22.sketch_text.stroke-77"),sQuery(id+"F15.wireOp",EDGE,"E22.sketch_text.stroke-78"),sQuery(id+"F15.wireOp",EDGE,"E22.sketch_text.stroke-79"),sQuery(id+"F15.wireOp",EDGE,"E22.sketch_text.stroke-80"),sQuery(id+"F15.wireOp",EDGE,"E22.sketch_text.stroke-81"),sQuery(id+"F15.wireOp",EDGE,"E22.sketch_text.stroke-82"),sQuery(id+"F15.wireOp",EDGE,"E22.sketch_text.stroke-83"),sQuery(id+"F15.wireOp",EDGE,"E22.sketch_text.stroke-84"),sQuery(id+"F15.wireOp",EDGE,"E22.sketch_text.stroke-85"),sQuery(id+"F15.wireOp",EDGE,"E22.sketch_text.stroke-86"),sQuery(id+"F15.wireOp",EDGE,"E22.sketch_text.stroke-87"),sQuery(id+"F15.wireOp",EDGE,"E22.sketch_text.stroke-88"),sQuery(id+"F15.wireOp",EDGE,"E22.sketch_text.stroke-89"),sQuery(id+"F15.wireOp",EDGE,"E22.sketch_text.stroke-90"),sQuery(id+"F15.wireOp",EDGE,"E22.sketch_text.stroke-91"),sQuery(id+"F15.wireOp",EDGE,"E22.sketch_text.stroke-92"),sQuery(id+"F15.wireOp",EDGE,"E22.sketch_text.stroke-93"),sQuery(id+"F15.wireOp",EDGE,"E22.sketch_text.stroke-94"),sQuery(id+"F15.wireOp",EDGE,"E22.sketch_text.stroke-95"),sQuery(id+"F15.wireOp",EDGE,"E22.sketch_text.stroke-96"),sQuery(id+"F15.wireOp",EDGE,"E22.sketch_text.stroke-97"),sQuery(id+"F15.wireOp",EDGE,"E22.sketch_text.stroke-98"),sQuery(id+"F15.wireOp",EDGE,"E22.sketch_text.stroke-99"),sQuery(id+"F15.wireOp",EDGE,"E22.sketch_text.stroke-100"),sQuery(id+"F15.wireOp",EDGE,"E22.sketch_text.stroke-101"),sQuery(id+"F15.wireOp",EDGE,"E22.sketch_text.stroke-102"),sQuery(id+"F15.wireOp",EDGE,"E22.sketch_text.stroke-103"),sQuery(id+"F15.wireOp",EDGE,"E22.sketch_text.stroke-104"),sQuery(id+"F15.wireOp",EDGE,"E22.sketch_text.stroke-105"),sQuery(id+"F15.wireOp",EDGE,"E22.sketch_text.stroke-106"),sQuery(id+"F15.wireOp",EDGE,"E22.sketch_text.stroke-107"),sQuery(id+"F15.wireOp",EDGE,"E22.sketch_text.stroke-108")])]});
            var Q2;
            Q2=makeQuery(id+"F16.opExtrude","SWEPT_BODY",BODY,{"disambiguationData":[OSD([sQuery(id+"F15.wireOp",EDGE,"E22.sketch_text.stroke-109"),sQuery(id+"F15.wireOp",EDGE,"E22.sketch_text.stroke-110"),sQuery(id+"F15.wireOp",EDGE,"E22.sketch_text.stroke-111"),sQuery(id+"F15.wireOp",EDGE,"E22.sketch_text.stroke-112"),sQuery(id+"F15.wireOp",EDGE,"E22.sketch_text.stroke-113"),sQuery(id+"F15.wireOp",EDGE,"E22.sketch_text.stroke-114"),sQuery(id+"F15.wireOp",EDGE,"E22.sketch_text.stroke-115"),sQuery(id+"F15.wireOp",EDGE,"E22.sketch_text.stroke-116"),sQuery(id+"F15.wireOp",EDGE,"E22.sketch_text.stroke-117"),sQuery(id+"F15.wireOp",EDGE,"E22.sketch_text.stroke-118"),sQuery(id+"F15.wireOp",EDGE,"E22.sketch_text.stroke-119"),sQuery(id+"F15.wireOp",EDGE,"E22.sketch_text.stroke-120"),sQuery(id+"F15.wireOp",EDGE,"E22.sketch_text.stroke-121"),sQuery(id+"F15.wireOp",EDGE,"E22.sketch_text.stroke-122"),sQuery(id+"F15.wireOp",EDGE,"E22.sketch_text.stroke-123"),sQuery(id+"F15.wireOp",EDGE,"E22.sketch_text.stroke-124"),sQuery(id+"F15.wireOp",EDGE,"E22.sketch_text.stroke-125"),sQuery(id+"F15.wireOp",EDGE,"E22.sketch_text.stroke-126"),sQuery(id+"F15.wireOp",EDGE,"E22.sketch_text.stroke-127"),sQuery(id+"F15.wireOp",EDGE,"E22.sketch_text.stroke-128"),sQuery(id+"F15.wireOp",EDGE,"E22.sketch_text.stroke-129"),sQuery(id+"F15.wireOp",EDGE,"E22.sketch_text.stroke-130"),sQuery(id+"F15.wireOp",EDGE,"E22.sketch_text.stroke-131"),sQuery(id+"F15.wireOp",EDGE,"E22.sketch_text.stroke-132"),sQuery(id+"F15.wireOp",EDGE,"E22.sketch_text.stroke-133"),sQuery(id+"F15.wireOp",EDGE,"E22.sketch_text.stroke-134"),sQuery(id+"F15.wireOp",EDGE,"E22.sketch_text.stroke-135"),sQuery(id+"F15.wireOp",EDGE,"E22.sketch_text.stroke-136"),sQuery(id+"F15.wireOp",EDGE,"E22.sketch_text.stroke-137"),sQuery(id+"F15.wireOp",EDGE,"E22.sketch_text.stroke-138"),sQuery(id+"F15.wireOp",EDGE,"E22.sketch_text.stroke-139"),sQuery(id+"F15.wireOp",EDGE,"E22.sketch_text.stroke-140"),sQuery(id+"F15.wireOp",EDGE,"E22.sketch_text.stroke-141"),sQuery(id+"F15.wireOp",EDGE,"E22.sketch_text.stroke-142"),sQuery(id+"F15.wireOp",EDGE,"E22.sketch_text.stroke-143"),sQuery(id+"F15.wireOp",EDGE,"E22.sketch_text.stroke-144"),sQuery(id+"F15.wireOp",EDGE,"E22.sketch_text.stroke-145"),sQuery(id+"F15.wireOp",EDGE,"E22.sketch_text.stroke-146"),sQuery(id+"F15.wireOp",EDGE,"E22.sketch_text.stroke-147"),sQuery(id+"F15.wireOp",EDGE,"E22.sketch_text.stroke-148"),sQuery(id+"F15.wireOp",EDGE,"E22.sketch_text.stroke-149"),sQuery(id+"F15.wireOp",EDGE,"E22.sketch_text.stroke-150"),sQuery(id+"F15.wireOp",EDGE,"E22.sketch_text.stroke-151"),sQuery(id+"F15.wireOp",EDGE,"E22.sketch_text.stroke-152"),sQuery(id+"F15.wireOp",EDGE,"E22.sketch_text.stroke-153"),sQuery(id+"F15.wireOp",EDGE,"E22.sketch_text.stroke-154"),sQuery(id+"F15.wireOp",EDGE,"E22.sketch_text.stroke-155"),sQuery(id+"F15.wireOp",EDGE,"E22.sketch_text.stroke-156"),sQuery(id+"F15.wireOp",EDGE,"E22.sketch_text.stroke-157"),sQuery(id+"F15.wireOp",EDGE,"E22.sketch_text.stroke-158")])]});
            transform(context, id + "F17", {"entities" : qUnion([Q0, Q1, Q2]), "transformType" : TransformType.TRANSLATION_3D, "dx" : -8.54 * mm, "dy" : -29.72 * mm, "dz" : -0.84 * mm, "makeCopy" : false});
        }
        {
            var Q0;
            Q0=makeQuery(id+"F16.opExtrude","CAP_FACE",FACE,{"disambiguationData":[OSD([sQuery(id+"F15.wireOp",EDGE,"E22.sketch_text.stroke-0"),sQuery(id+"F15.wireOp",EDGE,"E22.sketch_text.stroke-1"),sQuery(id+"F15.wireOp",EDGE,"E22.sketch_text.stroke-2"),sQuery(id+"F15.wireOp",EDGE,"E22.sketch_text.stroke-3"),sQuery(id+"F15.wireOp",EDGE,"E22.sketch_text.stroke-4"),sQuery(id+"F15.wireOp",EDGE,"E22.sketch_text.stroke-5"),sQuery(id+"F15.wireOp",EDGE,"E22.sketch_text.stroke-6"),sQuery(id+"F15.wireOp",EDGE,"E22.sketch_text.stroke-7"),sQuery(id+"F15.wireOp",EDGE,"E22.sketch_text.stroke-8"),sQuery(id+"F15.wireOp",EDGE,"E22.sketch_text.stroke-9"),sQuery(id+"F15.wireOp",EDGE,"E22.sketch_text.stroke-10"),sQuery(id+"F15.wireOp",EDGE,"E22.sketch_text.stroke-11"),sQuery(id+"F15.wireOp",EDGE,"E22.sketch_text.stroke-12"),sQuery(id+"F15.wireOp",EDGE,"E22.sketch_text.stroke-13"),sQuery(id+"F15.wireOp",EDGE,"E22.sketch_text.stroke-14"),sQuery(id+"F15.wireOp",EDGE,"E22.sketch_text.stroke-15"),sQuery(id+"F15.wireOp",EDGE,"E22.sketch_text.stroke-16"),sQuery(id+"F15.wireOp",EDGE,"E22.sketch_text.stroke-17"),sQuery(id+"F15.wireOp",EDGE,"E22.sketch_text.stroke-18"),sQuery(id+"F15.wireOp",EDGE,"E22.sketch_text.stroke-19"),sQuery(id+"F15.wireOp",EDGE,"E22.sketch_text.stroke-20"),sQuery(id+"F15.wireOp",EDGE,"E22.sketch_text.stroke-21"),sQuery(id+"F15.wireOp",EDGE,"E22.sketch_text.stroke-22"),sQuery(id+"F15.wireOp",EDGE,"E22.sketch_text.stroke-23"),sQuery(id+"F15.wireOp",EDGE,"E22.sketch_text.stroke-24"),sQuery(id+"F15.wireOp",EDGE,"E22.sketch_text.stroke-25"),sQuery(id+"F15.wireOp",EDGE,"E22.sketch_text.stroke-26"),sQuery(id+"F15.wireOp",EDGE,"E22.sketch_text.stroke-27"),sQuery(id+"F15.wireOp",EDGE,"E22.sketch_text.stroke-28"),sQuery(id+"F15.wireOp",EDGE,"E22.sketch_text.stroke-29"),sQuery(id+"F15.wireOp",EDGE,"E22.sketch_text.stroke-30"),sQuery(id+"F15.wireOp",EDGE,"E22.sketch_text.stroke-31"),sQuery(id+"F15.wireOp",EDGE,"E22.sketch_text.stroke-32"),sQuery(id+"F15.wireOp",EDGE,"E22.sketch_text.stroke-33"),sQuery(id+"F15.wireOp",EDGE,"E22.sketch_text.stroke-34"),sQuery(id+"F15.wireOp",EDGE,"E22.sketch_text.stroke-35"),sQuery(id+"F15.wireOp",EDGE,"E22.sketch_text.stroke-36"),sQuery(id+"F15.wireOp",EDGE,"E22.sketch_text.stroke-37"),sQuery(id+"F15.wireOp",EDGE,"E22.sketch_text.stroke-38"),sQuery(id+"F15.wireOp",EDGE,"E22.sketch_text.stroke-39"),sQuery(id+"F15.wireOp",EDGE,"E22.sketch_text.stroke-40"),sQuery(id+"F15.wireOp",EDGE,"E22.sketch_text.stroke-41"),sQuery(id+"F15.wireOp",EDGE,"E22.sketch_text.stroke-42"),sQuery(id+"F15.wireOp",EDGE,"E22.sketch_text.stroke-43"),sQuery(id+"F15.wireOp",EDGE,"E22.sketch_text.stroke-44"),sQuery(id+"F15.wireOp",EDGE,"E22.sketch_text.stroke-45"),sQuery(id+"F15.wireOp",EDGE,"E22.sketch_text.stroke-46"),sQuery(id+"F15.wireOp",EDGE,"E22.sketch_text.stroke-47"),sQuery(id+"F15.wireOp",EDGE,"E22.sketch_text.stroke-48"),sQuery(id+"F15.wireOp",EDGE,"E22.sketch_text.stroke-49"),sQuery(id+"F15.wireOp",EDGE,"E22.sketch_text.stroke-50"),sQuery(id+"F15.wireOp",EDGE,"E22.sketch_text.stroke-51"),sQuery(id+"F15.wireOp",EDGE,"E22.sketch_text.stroke-52"),sQuery(id+"F15.wireOp",EDGE,"E22.sketch_text.stroke-53"),sQuery(id+"F15.wireOp",EDGE,"E22.sketch_text.stroke-54"),sQuery(id+"F15.wireOp",EDGE,"E22.sketch_text.stroke-55"),sQuery(id+"F15.wireOp",EDGE,"E22.sketch_text.stroke-56"),sQuery(id+"F15.wireOp",EDGE,"E22.sketch_text.stroke-57"),sQuery(id+"F15.wireOp",EDGE,"E22.sketch_text.stroke-58"),sQuery(id+"F15.wireOp",EDGE,"E22.sketch_text.stroke-59")])],"isStart":false});
            var Q1;
            Q1=makeQuery(id+"F16.opExtrude","CAP_FACE",FACE,{"disambiguationData":[OSD([sQuery(id+"F15.wireOp",EDGE,"E22.sketch_text.stroke-109"),sQuery(id+"F15.wireOp",EDGE,"E22.sketch_text.stroke-110"),sQuery(id+"F15.wireOp",EDGE,"E22.sketch_text.stroke-111"),sQuery(id+"F15.wireOp",EDGE,"E22.sketch_text.stroke-112"),sQuery(id+"F15.wireOp",EDGE,"E22.sketch_text.stroke-113"),sQuery(id+"F15.wireOp",EDGE,"E22.sketch_text.stroke-114"),sQuery(id+"F15.wireOp",EDGE,"E22.sketch_text.stroke-115"),sQuery(id+"F15.wireOp",EDGE,"E22.sketch_text.stroke-116"),sQuery(id+"F15.wireOp",EDGE,"E22.sketch_text.stroke-117"),sQuery(id+"F15.wireOp",EDGE,"E22.sketch_text.stroke-118"),sQuery(id+"F15.wireOp",EDGE,"E22.sketch_text.stroke-119"),sQuery(id+"F15.wireOp",EDGE,"E22.sketch_text.stroke-120"),sQuery(id+"F15.wireOp",EDGE,"E22.sketch_text.stroke-121"),sQuery(id+"F15.wireOp",EDGE,"E22.sketch_text.stroke-122"),sQuery(id+"F15.wireOp",EDGE,"E22.sketch_text.stroke-123"),sQuery(id+"F15.wireOp",EDGE,"E22.sketch_text.stroke-124"),sQuery(id+"F15.wireOp",EDGE,"E22.sketch_text.stroke-125"),sQuery(id+"F15.wireOp",EDGE,"E22.sketch_text.stroke-126"),sQuery(id+"F15.wireOp",EDGE,"E22.sketch_text.stroke-127"),sQuery(id+"F15.wireOp",EDGE,"E22.sketch_text.stroke-128"),sQuery(id+"F15.wireOp",EDGE,"E22.sketch_text.stroke-129"),sQuery(id+"F15.wireOp",EDGE,"E22.sketch_text.stroke-130"),sQuery(id+"F15.wireOp",EDGE,"E22.sketch_text.stroke-131"),sQuery(id+"F15.wireOp",EDGE,"E22.sketch_text.stroke-132"),sQuery(id+"F15.wireOp",EDGE,"E22.sketch_text.stroke-133"),sQuery(id+"F15.wireOp",EDGE,"E22.sketch_text.stroke-134"),sQuery(id+"F15.wireOp",EDGE,"E22.sketch_text.stroke-135"),sQuery(id+"F15.wireOp",EDGE,"E22.sketch_text.stroke-136"),sQuery(id+"F15.wireOp",EDGE,"E22.sketch_text.stroke-137"),sQuery(id+"F15.wireOp",EDGE,"E22.sketch_text.stroke-138"),sQuery(id+"F15.wireOp",EDGE,"E22.sketch_text.stroke-139"),sQuery(id+"F15.wireOp",EDGE,"E22.sketch_text.stroke-140"),sQuery(id+"F15.wireOp",EDGE,"E22.sketch_text.stroke-141"),sQuery(id+"F15.wireOp",EDGE,"E22.sketch_text.stroke-142"),sQuery(id+"F15.wireOp",EDGE,"E22.sketch_text.stroke-143"),sQuery(id+"F15.wireOp",EDGE,"E22.sketch_text.stroke-144"),sQuery(id+"F15.wireOp",EDGE,"E22.sketch_text.stroke-145"),sQuery(id+"F15.wireOp",EDGE,"E22.sketch_text.stroke-146"),sQuery(id+"F15.wireOp",EDGE,"E22.sketch_text.stroke-147"),sQuery(id+"F15.wireOp",EDGE,"E22.sketch_text.stroke-148"),sQuery(id+"F15.wireOp",EDGE,"E22.sketch_text.stroke-149"),sQuery(id+"F15.wireOp",EDGE,"E22.sketch_text.stroke-150"),sQuery(id+"F15.wireOp",EDGE,"E22.sketch_text.stroke-151"),sQuery(id+"F15.wireOp",EDGE,"E22.sketch_text.stroke-152"),sQuery(id+"F15.wireOp",EDGE,"E22.sketch_text.stroke-153"),sQuery(id+"F15.wireOp",EDGE,"E22.sketch_text.stroke-154"),sQuery(id+"F15.wireOp",EDGE,"E22.sketch_text.stroke-155"),sQuery(id+"F15.wireOp",EDGE,"E22.sketch_text.stroke-156"),sQuery(id+"F15.wireOp",EDGE,"E22.sketch_text.stroke-157"),sQuery(id+"F15.wireOp",EDGE,"E22.sketch_text.stroke-158")])],"isStart":false});
            var Q2;
            Q2=makeQuery(id+"F16.opExtrude","CAP_FACE",FACE,{"disambiguationData":[OSD([sQuery(id+"F15.wireOp",EDGE,"E22.sketch_text.stroke-60"),sQuery(id+"F15.wireOp",EDGE,"E22.sketch_text.stroke-61"),sQuery(id+"F15.wireOp",EDGE,"E22.sketch_text.stroke-62"),sQuery(id+"F15.wireOp",EDGE,"E22.sketch_text.stroke-63"),sQuery(id+"F15.wireOp",EDGE,"E22.sketch_text.stroke-64"),sQuery(id+"F15.wireOp",EDGE,"E22.sketch_text.stroke-65"),sQuery(id+"F15.wireOp",EDGE,"E22.sketch_text.stroke-66"),sQuery(id+"F15.wireOp",EDGE,"E22.sketch_text.stroke-67"),sQuery(id+"F15.wireOp",EDGE,"E22.sketch_text.stroke-68"),sQuery(id+"F15.wireOp",EDGE,"E22.sketch_text.stroke-69"),sQuery(id+"F15.wireOp",EDGE,"E22.sketch_text.stroke-70"),sQuery(id+"F15.wireOp",EDGE,"E22.sketch_text.stroke-71"),sQuery(id+"F15.wireOp",EDGE,"E22.sketch_text.stroke-72"),sQuery(id+"F15.wireOp",EDGE,"E22.sketch_text.stroke-73"),sQuery(id+"F15.wireOp",EDGE,"E22.sketch_text.stroke-74"),sQuery(id+"F15.wireOp",EDGE,"E22.sketch_text.stroke-75"),sQuery(id+"F15.wireOp",EDGE,"E22.sketch_text.stroke-76"),sQuery(id+"F15.wireOp",EDGE,"E22.sketch_text.stroke-77"),sQuery(id+"F15.wireOp",EDGE,"E22.sketch_text.stroke-78"),sQuery(id+"F15.wireOp",EDGE,"E22.sketch_text.stroke-79"),sQuery(id+"F15.wireOp",EDGE,"E22.sketch_text.stroke-80"),sQuery(id+"F15.wireOp",EDGE,"E22.sketch_text.stroke-81"),sQuery(id+"F15.wireOp",EDGE,"E22.sketch_text.stroke-82"),sQuery(id+"F15.wireOp",EDGE,"E22.sketch_text.stroke-83"),sQuery(id+"F15.wireOp",EDGE,"E22.sketch_text.stroke-84"),sQuery(id+"F15.wireOp",EDGE,"E22.sketch_text.stroke-85"),sQuery(id+"F15.wireOp",EDGE,"E22.sketch_text.stroke-86"),sQuery(id+"F15.wireOp",EDGE,"E22.sketch_text.stroke-87"),sQuery(id+"F15.wireOp",EDGE,"E22.sketch_text.stroke-88"),sQuery(id+"F15.wireOp",EDGE,"E22.sketch_text.stroke-89"),sQuery(id+"F15.wireOp",EDGE,"E22.sketch_text.stroke-90"),sQuery(id+"F15.wireOp",EDGE,"E22.sketch_text.stroke-91"),sQuery(id+"F15.wireOp",EDGE,"E22.sketch_text.stroke-92"),sQuery(id+"F15.wireOp",EDGE,"E22.sketch_text.stroke-93"),sQuery(id+"F15.wireOp",EDGE,"E22.sketch_text.stroke-94"),sQuery(id+"F15.wireOp",EDGE,"E22.sketch_text.stroke-95"),sQuery(id+"F15.wireOp",EDGE,"E22.sketch_text.stroke-96"),sQuery(id+"F15.wireOp",EDGE,"E22.sketch_text.stroke-97"),sQuery(id+"F15.wireOp",EDGE,"E22.sketch_text.stroke-98"),sQuery(id+"F15.wireOp",EDGE,"E22.sketch_text.stroke-99"),sQuery(id+"F15.wireOp",EDGE,"E22.sketch_text.stroke-100"),sQuery(id+"F15.wireOp",EDGE,"E22.sketch_text.stroke-101"),sQuery(id+"F15.wireOp",EDGE,"E22.sketch_text.stroke-102"),sQuery(id+"F15.wireOp",EDGE,"E22.sketch_text.stroke-103"),sQuery(id+"F15.wireOp",EDGE,"E22.sketch_text.stroke-104"),sQuery(id+"F15.wireOp",EDGE,"E22.sketch_text.stroke-105"),sQuery(id+"F15.wireOp",EDGE,"E22.sketch_text.stroke-106"),sQuery(id+"F15.wireOp",EDGE,"E22.sketch_text.stroke-107"),sQuery(id+"F15.wireOp",EDGE,"E22.sketch_text.stroke-108")])],"isStart":false});
            fillet(context, id + "F18", {"entities" : qUnion([Q0, Q1, Q2]), "radius" : 0.13 * mm, "tangentPropagation" : true, "allowEdgeOverflow" : false});
        }
    });
